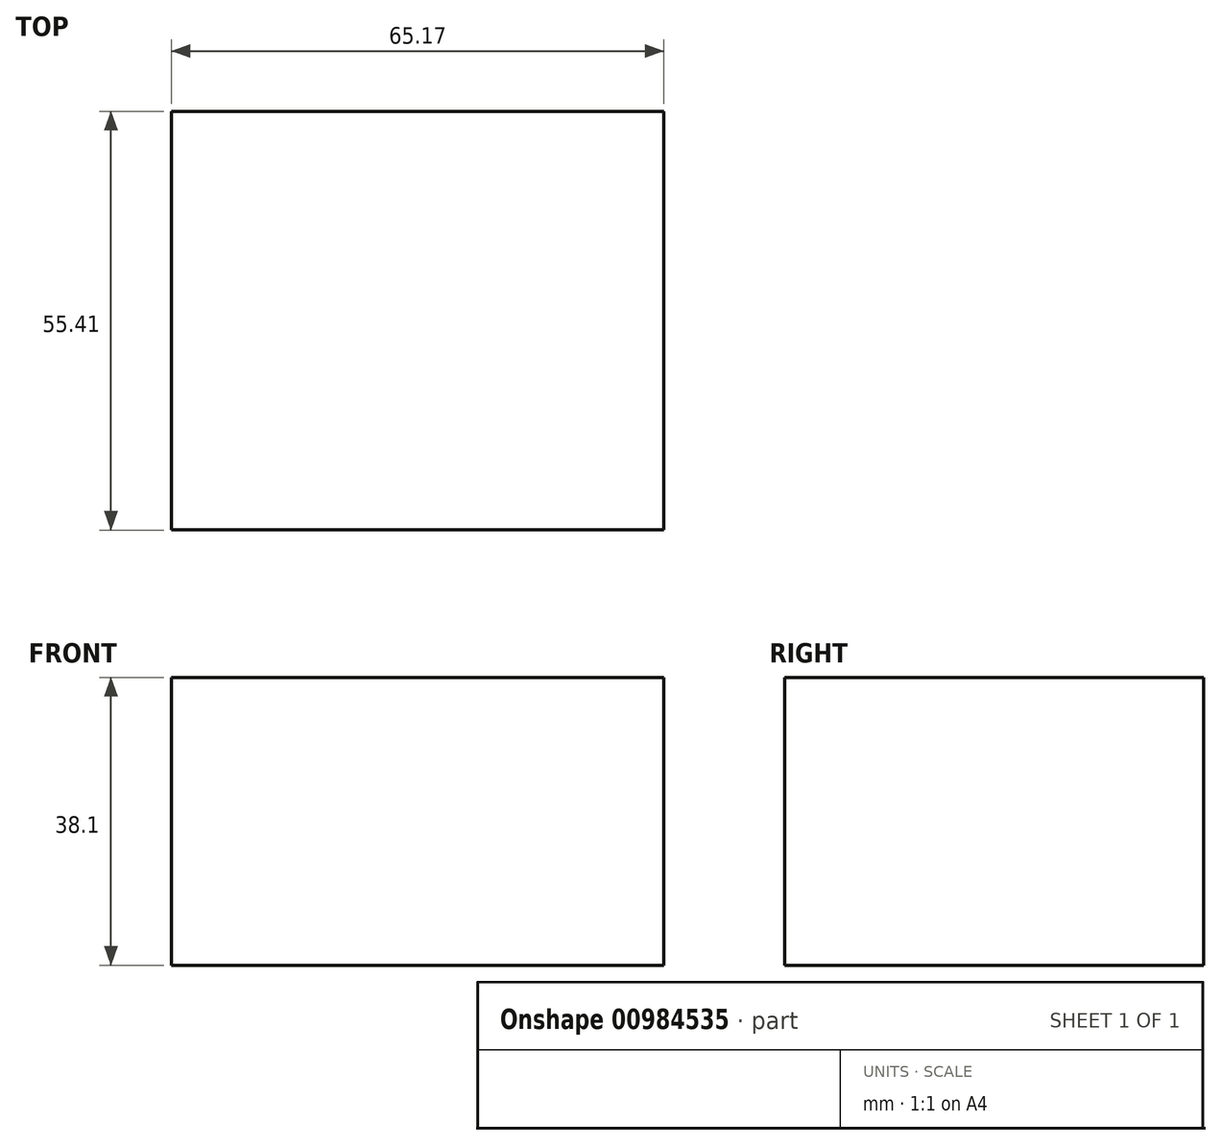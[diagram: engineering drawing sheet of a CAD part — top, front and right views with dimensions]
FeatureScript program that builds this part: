
annotation { "Feature Type Name" : "Feature", "Feature Type Description" : "" }
export const myFeature = defineFeature(function(context is Context, id is Id, definition is map)
    precondition{}
    {
        {
            var Q0;
            Q0=qCreatedBy(makeId("Top.planeOp"),FACE);
            var sketch = newSketch(context, id + "F0", { "sketchPlane" : qUnion([Q0])});
            skLineSegment(sketch, "E0.bottom", {"start": v(-30.4, 31.4) * mm, "end": v(34.76, 31.4) * mm});
            skLineSegment(sketch, "E0.top", {"start": v(-30.4, -24) * mm, "end": v(34.76, -24) * mm});
            skLineSegment(sketch, "E0.left", {"start": v(-30.4, 31.4) * mm, "end": v(-30.4, -24) * mm});
            skLineSegment(sketch, "E0.right", {"start": v(34.76, 31.4) * mm, "end": v(34.76, -24) * mm});
            skSolve(sketch);
        }
        {
            var Q0;
            Q0=makeQuery(id+"F0.imprint","IMPRINT",FACE,{"disambiguationData":[TD([[makeQuery(id+"F0.imprint","IMPRINT",EDGE,{"derivedFrom":sQuery(id+"F0.wireOp",EDGE,"E0.bottom")}),-1.0]])]});
            extrude(context, id + "F1", {"entities" : qUnion([Q0]), "depth" : 38.1 * mm, "offsetDistance" : 25.4 * mm});
        }
    });
